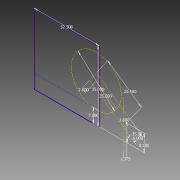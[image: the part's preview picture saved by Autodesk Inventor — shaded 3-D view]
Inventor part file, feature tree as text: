
AUTODESK INVENTOR PART (.ipt)
format: ipt  version: 2014 (Build 180170000, 170)  size: 75,264 bytes
history: native  units: in
note: dims shown in document units (in); Inventor stores cm internally (conversion verified against a paired STEP export)
features: sketch x1
ambient origin geometry x8: Origin, YZ Plane, XZ Plane, XY Plane, X Axis, Y Axis, Z Axis, Center Point
feature tree (1):
  sketch  "Sketch1"  dims[d0=32.5in d1=35.0in d2=7.0in d3=25.0in d5=6.0in d6=0.2405in d7=2.0in d8=20.5in d9=1.0in d10=8.5in d11=1.375in]
